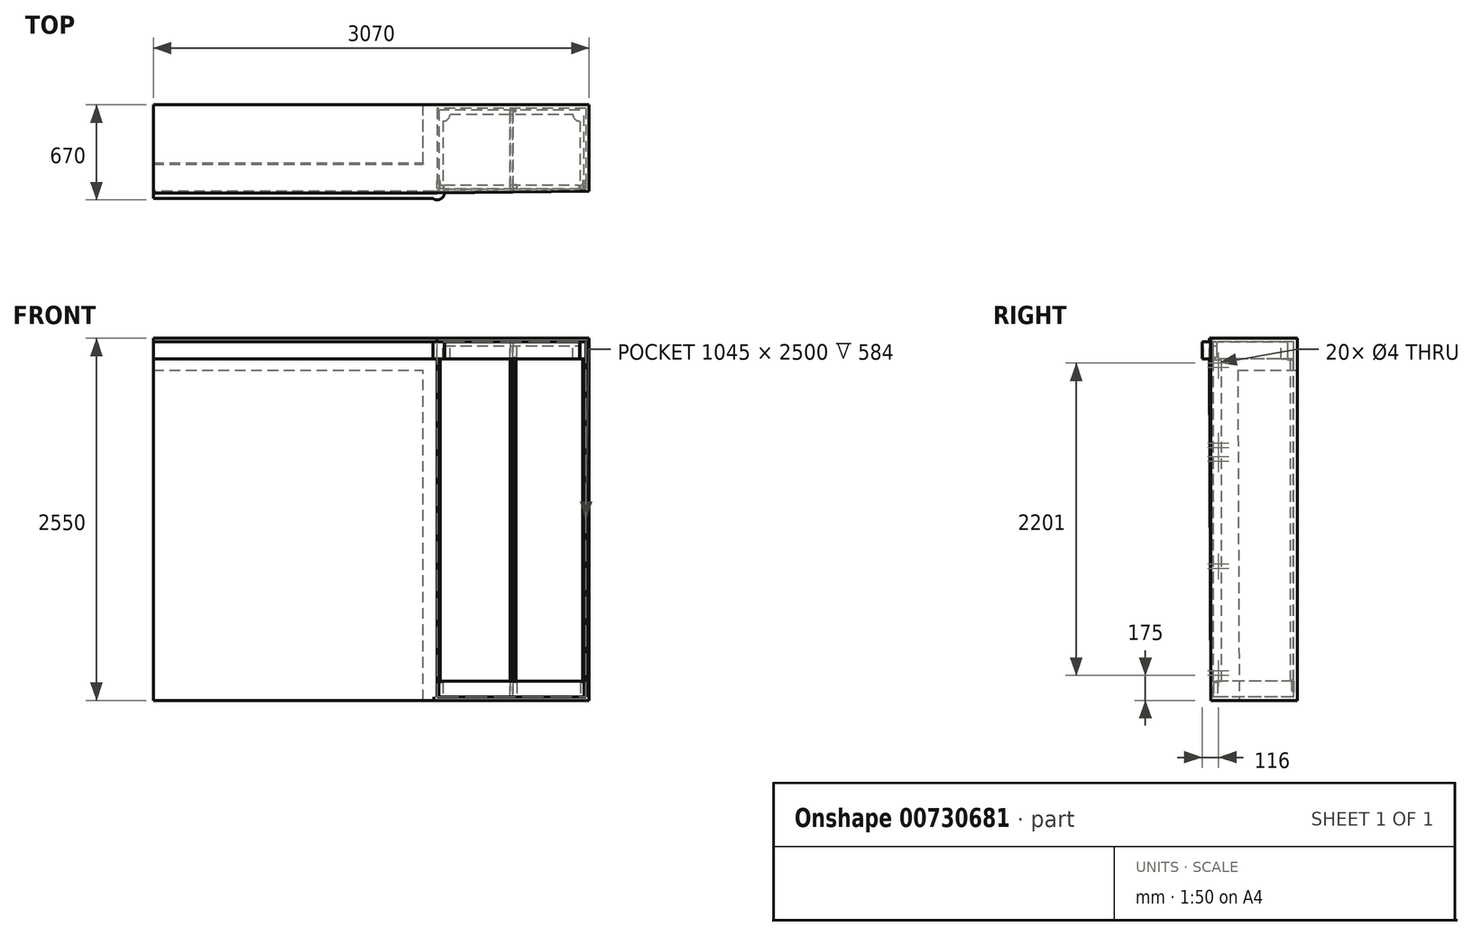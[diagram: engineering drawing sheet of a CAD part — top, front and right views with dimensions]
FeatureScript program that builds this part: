
annotation { "Feature Type Name" : "Feature", "Feature Type Description" : "" }
export const myFeature = defineFeature(function(context is Context, id is Id, definition is map)
    precondition{}
    {
        {
            var Q0;
            Q0=qCreatedBy(makeId("Top.planeOp"),FACE);
            var sketch = newSketch(context, id + "F0", { "sketchPlane" : qUnion([Q0])});
            skLineSegment(sketch, "E0.bottom", {"start": v(-522.5, 292) * mm, "end": v(522.5, 292) * mm});
            skLineSegment(sketch, "E0.top", {"start": v(-522.5, -292) * mm, "end": v(522.5, -292) * mm});
            skLineSegment(sketch, "E0.left", {"start": v(-522.5, 292) * mm, "end": v(-522.5, -292) * mm});
            skLineSegment(sketch, "E0.right", {"start": v(522.5, 292) * mm, "end": v(522.5, -292) * mm});
            skPoint(sketch, "E0.middle", {"position": v(0, 0) * mm});
            skSolve(sketch);
        }
        {
            var Q0;
            Q0 = qSketchRegion(id + "F0", true);
            extrude(context, id + "F1", {"entities" : qUnion([Q0]), "oppositeDirection" : true, "depth" : 25 * mm, "offsetDistance" : 25 * mm});
        }
        {
            var Q0;
            Q0=makeQuery(id+"F1.opExtrude","SWEPT_FACE",FACE,{"disambiguationData":[OSD([sQuery(id+"F0.wireOp",EDGE,"E0.left")])]});
            var sketch = newSketch(context, id + "F2", { "sketchPlane" : qUnion([Q0])});
            skLineSegment(sketch, "E1", {"start": v(-292, 0) * mm, "end": v(-292, 2500) * mm});
            skLineSegment(sketch, "E2", {"start": v(-292, 2500) * mm, "end": v(303, 2500) * mm});
            skLineSegment(sketch, "E3", {"start": v(303, 2500) * mm, "end": v(292, 0) * mm});
            skLineSegment(sketch, "E4", {"start": v(292, 0) * mm, "end": v(292, -25) * mm});
            skLineSegment(sketch, "E5", {"start": v(292, -25) * mm, "end": v(-292, -25) * mm});
            skLineSegment(sketch, "E6", {"start": v(-292, -25) * mm, "end": v(-292, 0) * mm});
            skSolve(sketch);
        }
        {
            var Q0;
            Q0 = qSketchRegion(id + "F2", true);
            extrude(context, id + "F3", {"entities" : qUnion([Q0]), "operationType" : NewBodyOperationType.ADD, "depth" : 25 * mm, "offsetDistance" : 25 * mm});
        }
        {
            var Q0;
            Q0=makeQuery(id+"F3.boolean.opBoolean","MERGE",FACE,{"derivedFrom":[makeQuery(id+"F1.opExtrude","SWEPT_FACE",FACE,{"disambiguationData":[OSD([sQuery(id+"F0.wireOp",EDGE,"E0.bottom")])]}),makeQuery(id+"F3.opExtrude","SWEPT_FACE",FACE,{"disambiguationData":[OSD([sQuery(id+"F2.wireOp",EDGE,"E1"),sQuery(id+"F2.wireOp",EDGE,"E6")])]})]});
            var sketch = newSketch(context, id + "F4", { "sketchPlane" : qUnion([Q0])});
            skLineSegment(sketch, "E7.bottom", {"start": v(522.5, 2500) * mm, "end": v(2522.5, 2500) * mm});
            skLineSegment(sketch, "E7.top", {"start": v(522.5, -25) * mm, "end": v(2522.5, -25) * mm});
            skLineSegment(sketch, "E7.left", {"start": v(522.5, 2500) * mm, "end": v(522.5, -25) * mm});
            skLineSegment(sketch, "E7.right", {"start": v(2522.5, 2500) * mm, "end": v(2522.5, -25) * mm});
            skSolve(sketch);
        }
        {
            var Q0;
            Q0 = qSketchRegion(id + "F4", true);
            var Q1;
            Q1=makeQuery(id+"F3.opExtrude","SWEPT_FACE",FACE,{"disambiguationData":[OSD([sQuery(id+"F2.wireOp",EDGE,"E3")])]});
            extrude(context, id + "F5", {"entities" : qUnion([Q0]), "operationType" : NewBodyOperationType.ADD, "endBound" : BoundingType.UP_TO_SURFACE, "oppositeDirection" : true, "depth" : 25 * mm, "endBoundEntityFace" : qUnion([Q1]), "offsetDistance" : 25 * mm});
        }
        {
            var Q0;
            Q0=makeQuery(id+"F1.opExtrude","SWEPT_FACE",FACE,{"disambiguationData":[OSD([sQuery(id+"F0.wireOp",EDGE,"E0.right")])]});
            var sketch = newSketch(context, id + "F6", { "sketchPlane" : qUnion([Q0])});
            skLineSegment(sketch, "E8.bottom", {"start": v(292, -25) * mm, "end": v(-292, -25) * mm});
            skLineSegment(sketch, "E8.top", {"start": v(292, 2500) * mm, "end": v(-292, 2500) * mm});
            skLineSegment(sketch, "E8.left", {"start": v(292, -25) * mm, "end": v(292, 2500) * mm});
            skLineSegment(sketch, "E8.right", {"start": v(-292, -25) * mm, "end": v(-292, 2500) * mm});
            skSolve(sketch);
        }
        {
            var Q0;
            Q0 = qSketchRegion(id + "F6", true);
            extrude(context, id + "F7", {"entities" : qUnion([Q0]), "operationType" : NewBodyOperationType.ADD, "depth" : 25 * mm, "offsetDistance" : 25 * mm});
        }
        {
            var Q0;
            Q0=makeQuery(id+"F7.boolean.opBoolean","MERGE",FACE,{"derivedFrom":[makeQuery(id+"F5.boolean.opBoolean","MERGE",FACE,{"derivedFrom":[makeQuery(id+"F3.boolean.opBoolean","MERGE",FACE,{"derivedFrom":[makeQuery(id+"F1.opExtrude","SWEPT_FACE",FACE,{"disambiguationData":[OSD([sQuery(id+"F0.wireOp",EDGE,"E0.bottom")])]}),makeQuery(id+"F3.opExtrude","SWEPT_FACE",FACE,{"disambiguationData":[OSD([sQuery(id+"F2.wireOp",EDGE,"E1"),sQuery(id+"F2.wireOp",EDGE,"E6")])]})]}),makeQuery(id+"F5.opExtrude","CAP_FACE",FACE,{"disambiguationData":[OSD([sQuery(id+"F4.wireOp",EDGE,"E7.bottom"),sQuery(id+"F4.wireOp",EDGE,"E7.top"),sQuery(id+"F4.wireOp",EDGE,"E7.left"),sQuery(id+"F4.wireOp",EDGE,"E7.right")])],"isStart":true})]}),makeQuery(id+"F7.opExtrude","SWEPT_FACE",FACE,{"disambiguationData":[OSD([sQuery(id+"F6.wireOp",EDGE,"E8.left")])]})]});
            var sketch = newSketch(context, id + "F8", { "sketchPlane" : qUnion([Q0])});
            skLineSegment(sketch, "E9.bottom", {"start": v(-547.5, 2500) * mm, "end": v(2522.5, 2500) * mm});
            skLineSegment(sketch, "E9.top", {"start": v(-547.5, -25) * mm, "end": v(2522.5, -25) * mm});
            skLineSegment(sketch, "E9.left", {"start": v(-547.5, 2500) * mm, "end": v(-547.5, -25) * mm});
            skLineSegment(sketch, "E9.right", {"start": v(2522.5, 2500) * mm, "end": v(2522.5, -25) * mm});
            skSolve(sketch);
        }
        {
            var Q0;
            Q0 = qSketchRegion(id + "F8", true);
            extrude(context, id + "F9", {"entities" : qUnion([Q0]), "operationType" : NewBodyOperationType.ADD, "depth" : 25 * mm, "offsetDistance" : 25 * mm});
        }
        {
            var Q0;
            Q0=makeQuery(id+"F9.boolean.opBoolean","MERGE",FACE,{"derivedFrom":[makeQuery(id+"F5.boolean.opBoolean","MERGE",FACE,{"derivedFrom":[makeQuery(id+"F3.opExtrude","SWEPT_FACE",FACE,{"disambiguationData":[OSD([sQuery(id+"F2.wireOp",EDGE,"E2")])]}),makeQuery(id+"F5.opExtrude","SWEPT_FACE",FACE,{"disambiguationData":[OSD([sQuery(id+"F4.wireOp",EDGE,"E7.bottom")])]})]}),makeQuery(id+"F7.opExtrude","SWEPT_FACE",FACE,{"disambiguationData":[OSD([sQuery(id+"F6.wireOp",EDGE,"E8.top")])]}),makeQuery(id+"F9.opExtrude","SWEPT_FACE",FACE,{"disambiguationData":[OSD([sQuery(id+"F8.wireOp",EDGE,"E9.bottom")])]})]});
            var sketch = newSketch(context, id + "F10", { "sketchPlane" : qUnion([Q0])});
            skLineSegment(sketch, "E10", {"start": v(547.5, -292) * mm, "end": v(-522.5, -303) * mm});
            skLineSegment(sketch, "E11", {"start": v(-522.5, -303) * mm, "end": v(-2522.5, -303) * mm});
            skLineSegment(sketch, "E12", {"start": v(-2522.5, -303) * mm, "end": v(-2522.5, 317) * mm});
            skLineSegment(sketch, "E13", {"start": v(-2522.5, 317) * mm, "end": v(547.5, 317) * mm});
            skLineSegment(sketch, "E14", {"start": v(547.5, 317) * mm, "end": v(547.5, -292) * mm});
            skSolve(sketch);
        }
        {
            var Q0;
            Q0 = qSketchRegion(id + "F10", true);
            extrude(context, id + "F11", {"entities" : qUnion([Q0]), "operationType" : NewBodyOperationType.ADD, "depth" : 25 * mm, "offsetDistance" : 25 * mm});
        }
        {
            var Q0;
            Q0=makeQuery(id+"F11.boolean.opBoolean","MERGE",FACE,{"derivedFrom":[makeQuery(id+"F9.opExtrude","CAP_FACE",FACE,{"disambiguationData":[OSD([sQuery(id+"F8.wireOp",EDGE,"E9.bottom"),sQuery(id+"F8.wireOp",EDGE,"E9.top"),sQuery(id+"F8.wireOp",EDGE,"E9.left"),sQuery(id+"F8.wireOp",EDGE,"E9.right")])],"isStart":false}),makeQuery(id+"F11.opExtrude","SWEPT_FACE",FACE,{"disambiguationData":[OSD([sQuery(id+"F10.wireOp",EDGE,"E13")])]})]});
            var sketch = newSketch(context, id + "F12", { "sketchPlane" : qUnion([Q0])});
            skLineSegment(sketch, "E15.bottom", {"start": v(2522.5, -25) * mm, "end": v(622.5, -25) * mm});
            skLineSegment(sketch, "E15.top", {"start": v(2522.5, 2300) * mm, "end": v(622.5, 2300) * mm});
            skLineSegment(sketch, "E15.left", {"start": v(2522.5, -25) * mm, "end": v(2522.5, 2300) * mm});
            skLineSegment(sketch, "E15.right", {"start": v(622.5, -25) * mm, "end": v(622.5, 2300) * mm});
            skSolve(sketch);
        }
        {
            var Q0;
            Q0 = qSketchRegion(id + "F12", true);
            var Q1;
            Q1=makeQuery(id+"F5.boolean.opBoolean","MERGE",FACE,{"derivedFrom":[makeQuery(id+"F3.opExtrude","SWEPT_FACE",FACE,{"disambiguationData":[OSD([sQuery(id+"F2.wireOp",EDGE,"E3")])]}),makeQuery(id+"F5.opExtrude","CAP_FACE",FACE,{"disambiguationData":[OSD([sQuery(id+"F4.wireOp",EDGE,"E7.bottom"),sQuery(id+"F4.wireOp",EDGE,"E7.top"),sQuery(id+"F4.wireOp",EDGE,"E7.left"),sQuery(id+"F4.wireOp",EDGE,"E7.right")])],"isStart":false})]});
            extrude(context, id + "F13", {"entities" : qUnion([Q0]), "operationType" : NewBodyOperationType.REMOVE, "endBound" : BoundingType.UP_TO_SURFACE, "oppositeDirection" : true, "depth" : 25 * mm, "endBoundEntityFace" : qUnion([Q1]), "hasOffset" : true, "offsetDistance" : 200 * mm});
        }
        {
            var Q0;
            Q0=makeQuery(id+"F1.opExtrude","CAP_FACE",FACE,{"disambiguationData":[OSD([sQuery(id+"F0.wireOp",EDGE,"E0.bottom"),sQuery(id+"F0.wireOp",EDGE,"E0.top"),sQuery(id+"F0.wireOp",EDGE,"E0.left"),sQuery(id+"F0.wireOp",EDGE,"E0.right")])],"isStart":true});
            var sketch = newSketch(context, id + "F14", { "sketchPlane" : qUnion([Q0])});
            skLineSegment(sketch, "E16.top", {"start": v(-522.5, -292) * mm, "end": v(-512.5, -292) * mm});
            skLineSegment(sketch, "E16.left", {"start": v(-522.5, 292) * mm, "end": v(-522.5, -292) * mm});
            skLineSegment(sketch, "E16.right", {"start": v(-512.5, 282) * mm, "end": v(-512.5, -292) * mm});
            skLineSegment(sketch, "E17.bottom", {"start": v(-522.5, 292) * mm, "end": v(522.5, 292) * mm});
            skLineSegment(sketch, "E17.top", {"start": v(-512.5, 282) * mm, "end": v(512.5, 282) * mm});
            skLineSegment(sketch, "E18.bottom", {"start": v(522.5, -292) * mm, "end": v(512.5, -292) * mm});
            skLineSegment(sketch, "E18.left", {"start": v(522.5, -292) * mm, "end": v(522.5, 292) * mm});
            skLineSegment(sketch, "E18.right", {"start": v(512.5, -292) * mm, "end": v(512.5, 282) * mm});
            skSolve(sketch);
        }
        {
            var Q0;
            Q0 = qSketchRegion(id + "F14", true);
            extrude(context, id + "F15", {"entities" : qUnion([Q0]), "depth" : 110 * mm, "offsetDistance" : 25 * mm});
        }
        {
            var Q0;
            Q0=makeQuery(id+"F11.opExtrude","CAP_FACE",FACE,{"disambiguationData":[OSD([sQuery(id+"F10.wireOp",EDGE,"E10"),sQuery(id+"F10.wireOp",EDGE,"E11"),sQuery(id+"F10.wireOp",EDGE,"E12"),sQuery(id+"F10.wireOp",EDGE,"E13"),sQuery(id+"F10.wireOp",EDGE,"E14")])],"isStart":true});
            var sketch = newSketch(context, id + "F16", { "sketchPlane" : qUnion([Q0])});
            skLineSegment(sketch, "E19.left", {"start": v(-522.5, -292) * mm, "end": v(-522.5, 303) * mm});
            skLineSegment(sketch, "E19.right", {"start": v(-482.5, -202) * mm, "end": v(-482.5, 273) * mm});
            skLineSegment(sketch, "E20.bottom", {"start": v(-522.5, -292) * mm, "end": v(522.5, -292) * mm});
            skLineSegment(sketch, "E20.top", {"start": v(-432.5, -252) * mm, "end": v(432.5, -252) * mm});
            skLineSegment(sketch, "E21.top", {"start": v(522.5, 292.67) * mm, "end": v(482.5, 292.67) * mm});
            skLineSegment(sketch, "E21.left", {"start": v(522.5, -292) * mm, "end": v(522.5, 292.67) * mm});
            skLineSegment(sketch, "E21.right", {"start": v(482.5, -202) * mm, "end": v(482.5, 292.67) * mm});
            skArc(sketch, "E22", {"start": v(-482.5, 273) * mm, "mid": v(-487.14, 338.36) * mm, "end": v(-552.5, 343) * mm});
            skArc(sketch, "E23", {"start": v(482.5, -202) * mm, "mid": v(447.14, -216.64) * mm, "end": v(432.5, -252) * mm});
            skArc(sketch, "E24.trimOffspring", {"start": v(-432.5, -252) * mm, "mid": v(-447.14, -216.64) * mm, "end": v(-482.5, -202) * mm});
            skLineSegment(sketch, "E25.bottom", {"start": v(-522.5, 303) * mm, "end": v(-2522.5, 303) * mm});
            skLineSegment(sketch, "E25.top", {"start": v(-552.5, 343) * mm, "end": v(-2522.5, 343) * mm});
            skLineSegment(sketch, "E25.right", {"start": v(-2522.5, 303) * mm, "end": v(-2522.5, 343) * mm});
            skSolve(sketch);
        }
        {
            var Q0;
            Q0 = qSketchRegion(id + "F16", true);
            extrude(context, id + "F17", {"entities" : qUnion([Q0]), "depth" : 120 * mm, "offsetDistance" : 25 * mm});
        }
        {
            var Q0;
            Q0=makeQuery(id+"F1.opExtrude","CAP_FACE",FACE,{"disambiguationData":[OSD([sQuery(id+"F0.wireOp",EDGE,"E0.bottom"),sQuery(id+"F0.wireOp",EDGE,"E0.top"),sQuery(id+"F0.wireOp",EDGE,"E0.left"),sQuery(id+"F0.wireOp",EDGE,"E0.right")])],"isStart":true});
            var sketch = newSketch(context, id + "F18", { "sketchPlane" : qUnion([Q0])});
            skLineSegment(sketch, "E26.bottom", {"start": v(-510, -274) * mm, "end": v(510, -274) * mm});
            skLineSegment(sketch, "E26.top", {"start": v(-510, -292) * mm, "end": v(510, -292) * mm});
            skLineSegment(sketch, "E26.left", {"start": v(-510, -274) * mm, "end": v(-510, -292) * mm});
            skLineSegment(sketch, "E26.right", {"start": v(510, -274) * mm, "end": v(510, -292) * mm});
            skSolve(sketch);
        }
        {
            var Q0;
            Q0 = qSketchRegion(id + "F18", true);
            var Q1;
            Q1=makeQuery(id+"F15.opExtrude","CAP_FACE",FACE,{"disambiguationData":[OSD([sQuery(id+"F14.wireOp",EDGE,"E16.top"),sQuery(id+"F14.wireOp",EDGE,"E16.left"),sQuery(id+"F14.wireOp",EDGE,"E16.right"),sQuery(id+"F14.wireOp",EDGE,"E17.bottom"),sQuery(id+"F14.wireOp",EDGE,"E17.top"),sQuery(id+"F14.wireOp",EDGE,"E18.bottom"),sQuery(id+"F14.wireOp",EDGE,"E18.left"),sQuery(id+"F14.wireOp",EDGE,"E18.right")])],"isStart":false});
            extrude(context, id + "F19", {"entities" : qUnion([Q0]), "endBound" : BoundingType.UP_TO_SURFACE, "depth" : 25 * mm, "endBoundEntityFace" : qUnion([Q1]), "offsetDistance" : 25 * mm});
        }
        {
            var Q0;
            Q0=makeQuery(id+"F11.opExtrude","CAP_FACE",FACE,{"disambiguationData":[OSD([sQuery(id+"F10.wireOp",EDGE,"E10"),sQuery(id+"F10.wireOp",EDGE,"E11"),sQuery(id+"F10.wireOp",EDGE,"E12"),sQuery(id+"F10.wireOp",EDGE,"E13"),sQuery(id+"F10.wireOp",EDGE,"E14")])],"isStart":true});
            var sketch = newSketch(context, id + "F20", { "sketchPlane" : qUnion([Q0])});
            skLineSegment(sketch, "E27.bottom", {"start": v(480, 292.7) * mm, "end": v(-470, 292.7) * mm});
            skLineSegment(sketch, "E27.top", {"start": v(480, 274.7) * mm, "end": v(-470, 274.7) * mm});
            skLineSegment(sketch, "E27.left", {"start": v(480, 292.7) * mm, "end": v(480, 274.7) * mm});
            skLineSegment(sketch, "E27.right", {"start": v(-470, 292.7) * mm, "end": v(-470, 274.7) * mm});
            skLineSegment(sketch, "E28", {"start": v(-472.5, 521.07) * mm, "end": v(-472.5, 254.4) * mm, "construction": true});
            skSolve(sketch);
        }
        {
            var Q0;
            Q0 = qSketchRegion(id + "F20", true);
            extrude(context, id + "F21", {"entities" : qUnion([Q0]), "depth" : 120 * mm, "offsetDistance" : 25 * mm});
        }
        {
            var Q0;
            Q0=makeQuery(id+"F3.opExtrude","CAP_FACE",FACE,{"disambiguationData":[OSD([sQuery(id+"F2.wireOp",EDGE,"E1"),sQuery(id+"F2.wireOp",EDGE,"E2"),sQuery(id+"F2.wireOp",EDGE,"E3"),sQuery(id+"F2.wireOp",EDGE,"E4"),sQuery(id+"F2.wireOp",EDGE,"E5"),sQuery(id+"F2.wireOp",EDGE,"E6")])],"isStart":true});
            var Q1;
            Q1=makeQuery(id+"F7.opExtrude","CAP_FACE",FACE,{"disambiguationData":[OSD([sQuery(id+"F6.wireOp",EDGE,"E8.bottom"),sQuery(id+"F6.wireOp",EDGE,"E8.top"),sQuery(id+"F6.wireOp",EDGE,"E8.left"),sQuery(id+"F6.wireOp",EDGE,"E8.right")])],"isStart":true});
            cPlane(context, id + "F22", {"entities" : qUnion([Q0, Q1]), "cplaneType" : CPlaneType.MID_PLANE, "offset" : 25 * mm, "width" : 150 * mm, "height" : 150 * mm});
        }
        {
            var Q0;
            Q0=qCreatedBy(id+"F22.planeOp",FACE);
            var sketch = newSketch(context, id + "F23", { "sketchPlane" : qUnion([Q0])});
            skLineSegment(sketch, "E29", {"start": v(287, 2375) * mm, "end": v(287, 115) * mm});
            skLineSegment(sketch, "E30", {"start": v(287, 115) * mm, "end": v(277, 115) * mm});
            skLineSegment(sketch, "E31", {"start": v(277, 115) * mm, "end": v(277, 0) * mm});
            skLineSegment(sketch, "E32", {"start": v(277, 0) * mm, "end": v(-274, 0) * mm});
            skLineSegment(sketch, "E33", {"start": v(-274, 0) * mm, "end": v(-274, 2500) * mm});
            skLineSegment(sketch, "E34", {"start": v(-274, 2500) * mm, "end": v(247, 2500) * mm});
            skLineSegment(sketch, "E35", {"start": v(247, 2500) * mm, "end": v(247, 2375) * mm});
            skLineSegment(sketch, "E36", {"start": v(247, 2375) * mm, "end": v(287, 2375) * mm});
            skSolve(sketch);
        }
        {
            var Q0;
            Q0=makeQuery(id+"F23.imprint","IMPRINT",FACE,{"disambiguationData":[TD([[makeQuery(id+"F23.imprint","IMPRINT",EDGE,{"derivedFrom":sQuery(id+"F23.wireOp",EDGE,"E29")}),-1.0]])]});
            extrude(context, id + "F24", {"entities" : qUnion([Q0]), "endBound" : BoundingType.SYMMETRIC, "depth" : 18 * mm, "offsetDistance" : 25 * mm});
        }
        {
            var Q0;
            Q0=makeQuery(id+"F3.opExtrude","CAP_FACE",FACE,{"disambiguationData":[OSD([sQuery(id+"F2.wireOp",EDGE,"E1"),sQuery(id+"F2.wireOp",EDGE,"E2"),sQuery(id+"F2.wireOp",EDGE,"E3"),sQuery(id+"F2.wireOp",EDGE,"E4"),sQuery(id+"F2.wireOp",EDGE,"E5"),sQuery(id+"F2.wireOp",EDGE,"E6")])],"isStart":true});
            var sketch = newSketch(context, id + "F25", { "sketchPlane" : qUnion([Q0])});
            skLineSegment(sketch, "E37.bottom", {"start": v(-274, 110) * mm, "end": v(-217, 110) * mm});
            skLineSegment(sketch, "E37.top", {"start": v(-274, 2375) * mm, "end": v(-217, 2375) * mm});
            skLineSegment(sketch, "E37.left", {"start": v(-274, 110) * mm, "end": v(-274, 2375) * mm});
            skLineSegment(sketch, "E37.right", {"start": v(-217, 110) * mm, "end": v(-217, 2375) * mm});
            skSolve(sketch);
        }
        {
            var Q0;
            Q0 = qSketchRegion(id + "F25", true);
            extrude(context, id + "F26", {"entities" : qUnion([Q0]), "depth" : 21 * mm, "offsetDistance" : 25 * mm});
        }
        {
            var Q0;
            Q0=makeQuery(id+"F7.opExtrude","CAP_FACE",FACE,{"disambiguationData":[OSD([sQuery(id+"F6.wireOp",EDGE,"E8.bottom"),sQuery(id+"F6.wireOp",EDGE,"E8.top"),sQuery(id+"F6.wireOp",EDGE,"E8.left"),sQuery(id+"F6.wireOp",EDGE,"E8.right")])],"isStart":true});
            var sketch = newSketch(context, id + "F27", { "sketchPlane" : qUnion([Q0])});
            skLineSegment(sketch, "E38.0.0", {"start": v(217, 2375) * mm, "end": v(274, 2375) * mm});
            skLineSegment(sketch, "E38.0.1", {"start": v(274, 2375) * mm, "end": v(274, 110) * mm});
            skLineSegment(sketch, "E38.0.2", {"start": v(274, 110) * mm, "end": v(217, 110) * mm});
            skLineSegment(sketch, "E38.0.3", {"start": v(217, 110) * mm, "end": v(217, 2375) * mm});
            skSolve(sketch);
        }
        {
            var Q0;
            Q0 = qSketchRegion(id + "F27", true);
            extrude(context, id + "F28", {"entities" : qUnion([Q0]), "depth" : 21 * mm, "offsetDistance" : 25 * mm});
        }
        {
            var Q0;
            Q0=makeQuery(id+"F9.opExtrude","CAP_FACE",FACE,{"disambiguationData":[OSD([sQuery(id+"F8.wireOp",EDGE,"E9.bottom"),sQuery(id+"F8.wireOp",EDGE,"E9.top"),sQuery(id+"F8.wireOp",EDGE,"E9.left"),sQuery(id+"F8.wireOp",EDGE,"E9.right")])],"isStart":true});
            var sketch = newSketch(context, id + "F29", { "sketchPlane" : qUnion([Q0])});
            skLineSegment(sketch, "E39.bottom", {"start": v(9, 110) * mm, "end": v(31, 110) * mm});
            skLineSegment(sketch, "E39.top", {"start": v(9, 2375) * mm, "end": v(31, 2375) * mm});
            skLineSegment(sketch, "E39.left", {"start": v(9, 110) * mm, "end": v(9, 2375) * mm});
            skLineSegment(sketch, "E39.right", {"start": v(31, 110) * mm, "end": v(31, 2375) * mm});
            skSolve(sketch);
        }
        {
            var Q0;
            Q0 = qSketchRegion(id + "F29", true);
            extrude(context, id + "F30", {"entities" : qUnion([Q0]), "depth" : 22 * mm, "offsetDistance" : 25 * mm});
        }
        {
            var Q0;
            Q0=makeQuery(id+"F1.opExtrude","CAP_FACE",FACE,{"disambiguationData":[OSD([sQuery(id+"F0.wireOp",EDGE,"E0.bottom"),sQuery(id+"F0.wireOp",EDGE,"E0.top"),sQuery(id+"F0.wireOp",EDGE,"E0.left"),sQuery(id+"F0.wireOp",EDGE,"E0.right")])],"isStart":true});
            var sketch = newSketch(context, id + "F31", { "sketchPlane" : qUnion([Q0])});
            skLineSegment(sketch, "E40.bottom", {"start": v(-510, -246) * mm, "end": v(-482, -246) * mm});
            skLineSegment(sketch, "E40.top", {"start": v(-510, -274) * mm, "end": v(-482, -274) * mm});
            skLineSegment(sketch, "E40.left", {"start": v(-510, -246) * mm, "end": v(-510, -274) * mm});
            skLineSegment(sketch, "E40.right", {"start": v(-482, -246) * mm, "end": v(-482, -274) * mm});
            skLineSegment(sketch, "E41.bottom", {"start": v(37, -246) * mm, "end": v(9, -246) * mm});
            skLineSegment(sketch, "E41.top", {"start": v(37, -274) * mm, "end": v(9, -274) * mm});
            skLineSegment(sketch, "E41.left", {"start": v(37, -246) * mm, "end": v(37, -274) * mm});
            skLineSegment(sketch, "E41.right", {"start": v(9, -246) * mm, "end": v(9, -274) * mm});
            skLineSegment(sketch, "E42.bottom", {"start": v(484.5, -246) * mm, "end": v(512.5, -246) * mm});
            skLineSegment(sketch, "E42.top", {"start": v(484.5, -274) * mm, "end": v(512.5, -274) * mm});
            skLineSegment(sketch, "E42.left", {"start": v(484.5, -246) * mm, "end": v(484.5, -274) * mm});
            skLineSegment(sketch, "E42.right", {"start": v(512.5, -246) * mm, "end": v(512.5, -274) * mm});
            skSolve(sketch);
        }
        {
            var Q0;
            Q0 = qSketchRegion(id + "F31", true);
            extrude(context, id + "F32", {"entities" : qUnion([Q0]), "depth" : 100 * mm, "offsetDistance" : 25 * mm});
        }
        {
            var Q0;
            Q0=makeQuery(id+"F11.opExtrude","CAP_FACE",FACE,{"disambiguationData":[OSD([sQuery(id+"F10.wireOp",EDGE,"E10"),sQuery(id+"F10.wireOp",EDGE,"E11"),sQuery(id+"F10.wireOp",EDGE,"E12"),sQuery(id+"F10.wireOp",EDGE,"E13"),sQuery(id+"F10.wireOp",EDGE,"E14")])],"isStart":true});
            var sketch = newSketch(context, id + "F33", { "sketchPlane" : qUnion([Q0])});
            skLineSegment(sketch, "E43.bottom", {"start": v(-472.5, 274.7) * mm, "end": v(477.5, 274.7) * mm});
            skLineSegment(sketch, "E43.top", {"start": v(-472.5, 246.7) * mm, "end": v(477.5, 246.7) * mm});
            skLineSegment(sketch, "E43.left", {"start": v(-472.5, 274.7) * mm, "end": v(-472.5, 246.7) * mm});
            skLineSegment(sketch, "E43.right", {"start": v(477.5, 274.7) * mm, "end": v(477.5, 246.7) * mm});
            skSolve(sketch);
        }
        {
            var Q0;
            Q0 = qSketchRegion(id + "F33", true);
            extrude(context, id + "F34", {"entities" : qUnion([Q0]), "depth" : 28 * mm, "offsetDistance" : 25 * mm});
        }
        {
            var Q0;
            Q0=makeQuery(id+"F34.opExtrude","CAP_FACE",FACE,{"disambiguationData":[OSD([sQuery(id+"F33.wireOp",EDGE,"E43.bottom"),sQuery(id+"F33.wireOp",EDGE,"E43.top"),sQuery(id+"F33.wireOp",EDGE,"E43.left"),sQuery(id+"F33.wireOp",EDGE,"E43.right")])],"isStart":false});
            var sketch = newSketch(context, id + "F35", { "sketchPlane" : qUnion([Q0])});
            skLineSegment(sketch, "E44.bottom", {"start": v(9, 274.7) * mm, "end": v(37, 274.7) * mm});
            skLineSegment(sketch, "E44.top", {"start": v(9, 246.7) * mm, "end": v(37, 246.7) * mm});
            skLineSegment(sketch, "E44.left", {"start": v(9, 274.7) * mm, "end": v(9, 246.7) * mm});
            skLineSegment(sketch, "E44.right", {"start": v(37, 274.7) * mm, "end": v(37, 246.7) * mm});
            skSolve(sketch);
        }
        {
            var Q0;
            Q0 = qSketchRegion(id + "F35", true);
            extrude(context, id + "F36", {"entities" : qUnion([Q0]), "depth" : 80 * mm, "offsetDistance" : 25 * mm});
        }
        {
            var Q0;
            Q0=makeQuery(id+"F26.opExtrude","CAP_FACE",FACE,{"disambiguationData":[OSD([sQuery(id+"F25.wireOp",EDGE,"E37.bottom"),sQuery(id+"F25.wireOp",EDGE,"E37.top"),sQuery(id+"F25.wireOp",EDGE,"E37.left"),sQuery(id+"F25.wireOp",EDGE,"E37.right")])],"isStart":false});
            var sketch = newSketch(context, id + "F37", { "sketchPlane" : qUnion([Q0])});
            skCircle(sketch, "E45", {"center": v(-237, 2351) * mm, "radius": 2 * mm});
            skCircle(sketch, "E46", {"center": v(-237, 2319) * mm, "radius": 2 * mm});
            skCircle(sketch, "E47.0.1.0", {"center": v(-237, 1787) * mm, "radius": 2 * mm});
            skCircle(sketch, "E47.0.1.1", {"center": v(-237, 1755) * mm, "radius": 2 * mm});
            skLineSegment(sketch, "E47.direction1", {"start": v(-237, 2351) * mm, "end": v(-214, 2351) * mm, "construction": true});
            skLineSegment(sketch, "E47.direction2", {"start": v(-237, 2351) * mm, "end": v(-237, 1787) * mm, "construction": true});
            skSolve(sketch);
        }
        {
            var Q0;
            Q0 = qSketchRegion(id + "F37", true);
            extrude(context, id + "F38", {"entities" : qUnion([Q0]), "operationType" : NewBodyOperationType.REMOVE, "endBound" : BoundingType.UP_TO_NEXT, "oppositeDirection" : true, "depth" : 25 * mm, "offsetDistance" : 25 * mm});
        }
        {
            var Q0;
            Q0=makeQuery(id+"F26.opExtrude","CAP_FACE",FACE,{"disambiguationData":[OSD([sQuery(id+"F25.wireOp",EDGE,"E37.bottom"),sQuery(id+"F25.wireOp",EDGE,"E37.top"),sQuery(id+"F25.wireOp",EDGE,"E37.left"),sQuery(id+"F25.wireOp",EDGE,"E37.right")])],"isStart":false});
            var sketch = newSketch(context, id + "F39", { "sketchPlane" : qUnion([Q0])});
            skCircle(sketch, "E48", {"center": v(-237, 182) * mm, "radius": 2 * mm});
            skCircle(sketch, "E49", {"center": v(-237, 150) * mm, "radius": 2 * mm});
            skLineSegment(sketch, "E50", {"start": v(-237, 182) * mm, "end": v(-237, 150) * mm, "construction": true});
            skCircle(sketch, "E51.0.1.0", {"center": v(-237, 937) * mm, "radius": 2 * mm});
            skCircle(sketch, "E51.0.1.1", {"center": v(-237, 905) * mm, "radius": 2 * mm});
            skCircle(sketch, "E51.0.2.0", {"center": v(-237, 1692) * mm, "radius": 2 * mm});
            skCircle(sketch, "E51.0.2.1", {"center": v(-237, 1660) * mm, "radius": 2 * mm});
            skLineSegment(sketch, "E51.direction1", {"start": v(-237, 182) * mm, "end": v(-214, 182) * mm, "construction": true});
            skLineSegment(sketch, "E51.direction2", {"start": v(-237, 182) * mm, "end": v(-237, 937) * mm, "construction": true});
            skSolve(sketch);
        }
        {
            var Q0;
            Q0 = qSketchRegion(id + "F39", true);
            extrude(context, id + "F40", {"entities" : qUnion([Q0]), "operationType" : NewBodyOperationType.REMOVE, "endBound" : BoundingType.UP_TO_NEXT, "oppositeDirection" : true, "depth" : 25 * mm, "offsetDistance" : 25 * mm});
        }
        {
            var Q0;
            Q0=makeQuery(id+"F28.opExtrude","CAP_FACE",FACE,{"disambiguationData":[OSD([sQuery(id+"F27.wireOp",EDGE,"E38.0.0"),sQuery(id+"F27.wireOp",EDGE,"E38.0.1"),sQuery(id+"F27.wireOp",EDGE,"E38.0.2"),sQuery(id+"F27.wireOp",EDGE,"E38.0.3")])],"isStart":false});
            var sketch = newSketch(context, id + "F41", { "sketchPlane" : qUnion([Q0])});
            skCircle(sketch, "E52.0", {"center": v(237, 2351) * mm, "radius": 2 * mm});
            skCircle(sketch, "E53.0", {"center": v(237, 2319) * mm, "radius": 2 * mm});
            skCircle(sketch, "E54.0", {"center": v(237, 1787) * mm, "radius": 2 * mm});
            skCircle(sketch, "E55.0", {"center": v(237, 1755) * mm, "radius": 2 * mm});
            skCircle(sketch, "E56.0", {"center": v(237, 1692) * mm, "radius": 2 * mm});
            skCircle(sketch, "E57.0", {"center": v(237, 1660) * mm, "radius": 2 * mm});
            skCircle(sketch, "E58.0", {"center": v(237, 937) * mm, "radius": 2 * mm});
            skCircle(sketch, "E59.0", {"center": v(237, 905) * mm, "radius": 2 * mm});
            skCircle(sketch, "E60.0", {"center": v(237, 182) * mm, "radius": 2 * mm});
            skCircle(sketch, "E61.0", {"center": v(237, 150) * mm, "radius": 2 * mm});
            skSolve(sketch);
        }
        {
            var Q0;
            Q0 = qSketchRegion(id + "F41", true);
            extrude(context, id + "F42", {"entities" : qUnion([Q0]), "operationType" : NewBodyOperationType.REMOVE, "endBound" : BoundingType.UP_TO_NEXT, "oppositeDirection" : true, "depth" : 25 * mm, "offsetDistance" : 25 * mm});
        }
        {
            var Q0;
            Q0=makeQuery(id+"F3.opExtrude","CAP_FACE",FACE,{"disambiguationData":[OSD([sQuery(id+"F2.wireOp",EDGE,"E1"),sQuery(id+"F2.wireOp",EDGE,"E2"),sQuery(id+"F2.wireOp",EDGE,"E3"),sQuery(id+"F2.wireOp",EDGE,"E4"),sQuery(id+"F2.wireOp",EDGE,"E5"),sQuery(id+"F2.wireOp",EDGE,"E6")])],"isStart":true});
            var sketch = newSketch(context, id + "F43", { "sketchPlane" : qUnion([Q0])});
            skLineSegment(sketch, "E62", {"start": v(-217, 1598) * mm, "end": v(292, 1598) * mm});
            skPoint(sketch, "E63", {"position": v(37.5, 1598) * mm});
            skSolve(sketch);
        }
    });
